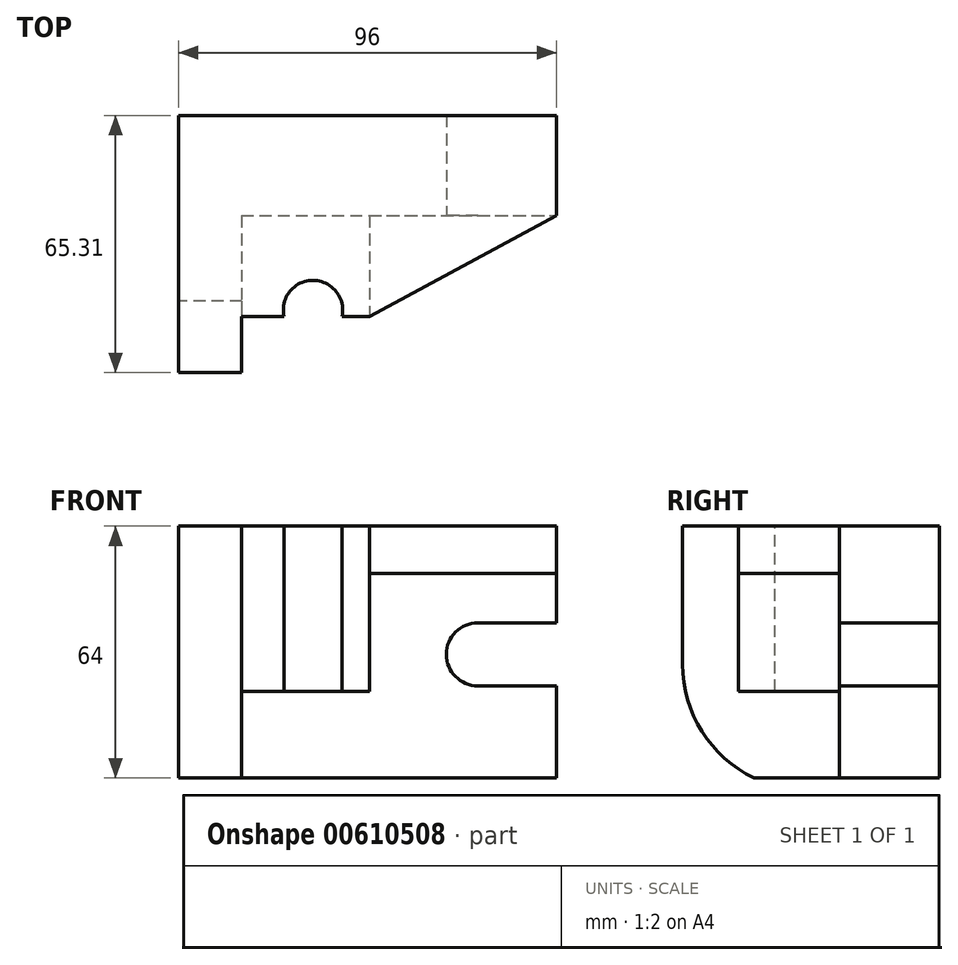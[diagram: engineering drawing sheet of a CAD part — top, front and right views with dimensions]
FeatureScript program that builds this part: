
annotation { "Feature Type Name" : "Feature", "Feature Type Description" : "" }
export const myFeature = defineFeature(function(context is Context, id is Id, definition is map)
    precondition{}
    {
        {
            var Q0;
            Q0=qCreatedBy(makeId("Front.planeOp"),FACE);
            var sketch = newSketch(context, id + "F0", { "sketchPlane" : qUnion([Q0])});
            skLineSegment(sketch, "E0.bottom", {"start": v(-48.48, 24.6) * mm, "end": v(47.52, 24.6) * mm});
            skLineSegment(sketch, "E0.top", {"start": v(-48.48, -39.4) * mm, "end": v(47.52, -39.4) * mm});
            skLineSegment(sketch, "E0.left", {"start": v(-48.48, 24.6) * mm, "end": v(-48.48, -39.4) * mm});
            skLineSegment(sketch, "E0.right", {"start": v(47.52, 24.6) * mm, "end": v(47.52, -39.4) * mm});
            skSolve(sketch);
        }
        {
            var Q0;
            Q0 = qSketchRegion(id + "F0", true);
            extrude(context, id + "F1", {"entities" : qUnion([Q0]), "depth" : 25.4 * mm, "offsetDistance" : 25.4 * mm});
        }
        {
            var Q0;
            Q0=makeQuery(id+"F1.opExtrude","CAP_FACE",FACE,{"disambiguationData":[OSD([sQuery(id+"F0.wireOp",EDGE,"E0.bottom"),sQuery(id+"F0.wireOp",EDGE,"E0.top"),sQuery(id+"F0.wireOp",EDGE,"E0.left"),sQuery(id+"F0.wireOp",EDGE,"E0.right")])],"isStart":false});
            var sketch = newSketch(context, id + "F2", { "sketchPlane" : qUnion([Q0])});
            skLineSegment(sketch, "E1.bottom", {"start": v(27.52, 0) * mm, "end": v(47.52, 0) * mm});
            skLineSegment(sketch, "E1.top", {"start": v(27.52, -16) * mm, "end": v(47.52, -16) * mm});
            skLineSegment(sketch, "E1.left", {"start": v(27.52, 0) * mm, "end": v(27.52, -16) * mm});
            skLineSegment(sketch, "E1.right", {"start": v(47.52, 0) * mm, "end": v(47.52, -16) * mm});
            skArc(sketch, "E2", {"start": v(27.52, 0) * mm, "mid": v(19.52, -8) * mm, "end": v(27.52, -16) * mm});
            skSolve(sketch);
        }
        {
            var Q0;
            Q0=makeQuery(id+"F2.imprint","IMPRINT",FACE,{"disambiguationData":[TD([[makeQuery(id+"F2.imprint","IMPRINT",EDGE,{"derivedFrom":sQuery(id+"F2.wireOp",EDGE,"E1.left")}),-1.0]])]});
            var Q1;
            Q1=makeQuery(id+"F2.imprint","IMPRINT",FACE,{"disambiguationData":[TD([[makeQuery(id+"F2.imprint","IMPRINT",EDGE,{"derivedFrom":sQuery(id+"F2.wireOp",EDGE,"E1.bottom")}),-1.0]])]});
            extrude(context, id + "F3", {"entities" : qUnion([Q0, Q1]), "operationType" : NewBodyOperationType.REMOVE, "oppositeDirection" : true, "depth" : 25.4 * mm, "offsetDistance" : 25.4 * mm});
        }
        {
            var Q0;
            Q0=makeQuery(id+"F1.opExtrude","SWEPT_FACE",FACE,{"disambiguationData":[OSD([sQuery(id+"F0.wireOp",EDGE,"E0.left")])]});
            var sketch = newSketch(context, id + "F4", { "sketchPlane" : qUnion([Q0])});
            skLineSegment(sketch, "E3", {"start": v(25.4, 24.6) * mm, "end": v(65.31, 24.6) * mm});
            skLineSegment(sketch, "E4", {"start": v(65.31, 24.6) * mm, "end": v(65.31, -10.53) * mm});
            skLineSegment(sketch, "E5", {"start": v(25.4, 24.6) * mm, "end": v(25.4, -39.4) * mm});
            skLineSegment(sketch, "E6", {"start": v(25.4, -39.4) * mm, "end": v(47.1, -39.4) * mm});
            skArc(sketch, "E7", {"start": v(47.1, -39.4) * mm, "mid": v(60.38, -27.6) * mm, "end": v(65.31, -10.53) * mm});
            skSolve(sketch);
        }
        {
            var Q0;
            Q0=makeQuery(id+"F4.imprint","IMPRINT",FACE,{"disambiguationData":[TD([[makeQuery(id+"F4.imprint","IMPRINT",EDGE,{"derivedFrom":sQuery(id+"F4.wireOp",EDGE,"E3")}),-1.0]])]});
            extrude(context, id + "F5", {"entities" : qUnion([Q0]), "operationType" : NewBodyOperationType.ADD, "oppositeDirection" : true, "depth" : 16 * mm, "offsetDistance" : 25.4 * mm});
        }
        {
            var Q0;
            Q0=makeQuery(id+"F5.boolean.opBoolean","MERGE",FACE,{"derivedFrom":[makeQuery(id+"F1.opExtrude","SWEPT_FACE",FACE,{"disambiguationData":[OSD([sQuery(id+"F0.wireOp",EDGE,"E0.bottom")])]}),makeQuery(id+"F5.opExtrude","SWEPT_FACE",FACE,{"disambiguationData":[OSD([sQuery(id+"F4.wireOp",EDGE,"E3")])]})]});
            var sketch = newSketch(context, id + "F6", { "sketchPlane" : qUnion([Q0])});
            skLineSegment(sketch, "E8", {"start": v(-32.48, -25.4) * mm, "end": v(-32.48, -51.1) * mm});
            skLineSegment(sketch, "E9", {"start": v(-32.48, -51.1) * mm, "end": v(-21.7, -51.1) * mm});
            skLineSegment(sketch, "E10", {"start": v(-32.48, -25.4) * mm, "end": v(0, -25.4) * mm});
            skLineSegment(sketch, "E11", {"start": v(0, -25.4) * mm, "end": v(0, -51.1) * mm});
            skLineSegment(sketch, "E12", {"start": v(0, -51.1) * mm, "end": v(-7, -51.1) * mm});
            skArc(sketch, "E13", {"start": v(-7, -51.1) * mm, "mid": v(-14.35, -41.87) * mm, "end": v(-21.7, -51.1) * mm});
            skSolve(sketch);
        }
        {
            var Q0;
            Q0 = qSketchRegion(id + "F6", true);
            extrude(context, id + "F7", {"entities" : qUnion([Q0]), "operationType" : NewBodyOperationType.ADD, "oppositeDirection" : true, "depth" : 42 * mm, "offsetDistance" : 25.4 * mm});
        }
        {
            var Q0;
            Q0=makeQuery(id+"F7.boolean.opBoolean","MERGE",FACE,{"derivedFrom":[makeQuery(id+"F5.boolean.opBoolean","MERGE",FACE,{"derivedFrom":[makeQuery(id+"F1.opExtrude","SWEPT_FACE",FACE,{"disambiguationData":[OSD([sQuery(id+"F0.wireOp",EDGE,"E0.bottom")])]}),makeQuery(id+"F5.opExtrude","SWEPT_FACE",FACE,{"disambiguationData":[OSD([sQuery(id+"F4.wireOp",EDGE,"E3")])]})]}),makeQuery(id+"F7.opExtrude","CAP_FACE",FACE,{"disambiguationData":[OSD([sQuery(id+"F6.wireOp",EDGE,"E8"),sQuery(id+"F6.wireOp",EDGE,"E9"),sQuery(id+"F6.wireOp",EDGE,"E10"),sQuery(id+"F6.wireOp",EDGE,"E11"),sQuery(id+"F6.wireOp",EDGE,"E12"),sQuery(id+"F6.wireOp",EDGE,"E13")])],"isStart":true})]});
            var sketch = newSketch(context, id + "F8", { "sketchPlane" : qUnion([Q0])});
            skLineSegment(sketch, "E14", {"start": v(47.52, -25.4) * mm, "end": v(0, -51.1) * mm});
            skLineSegment(sketch, "E15", {"start": v(0, -51.1) * mm, "end": v(0, -25.4) * mm});
            skLineSegment(sketch, "E16", {"start": v(0, -25.4) * mm, "end": v(47.52, -25.4) * mm});
            skSolve(sketch);
        }
        {
            var Q0;
            Q0 = qSketchRegion(id + "F8", true);
            extrude(context, id + "F9", {"entities" : qUnion([Q0]), "operationType" : NewBodyOperationType.ADD, "oppositeDirection" : true, "depth" : 12 * mm, "offsetDistance" : 25.4 * mm});
        }
    });
